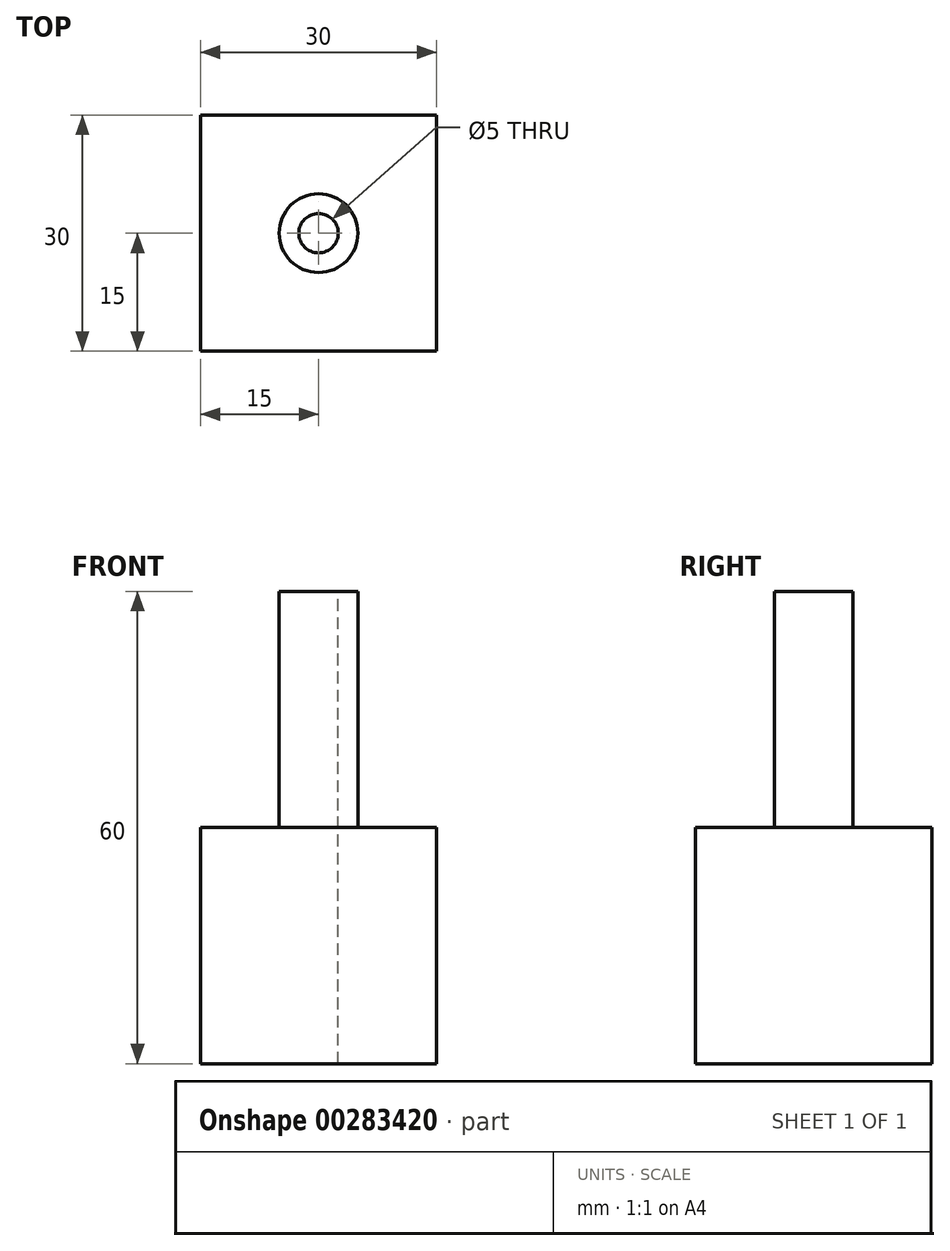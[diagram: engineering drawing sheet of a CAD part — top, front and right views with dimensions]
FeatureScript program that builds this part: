
annotation { "Feature Type Name" : "Feature", "Feature Type Description" : "" }
export const myFeature = defineFeature(function(context is Context, id is Id, definition is map)
    precondition{}
    {
        {
            var Q0;
            Q0=qCreatedBy(makeId("Top.planeOp"),FACE);
            var sketch = newSketch(context, id + "F0", { "sketchPlane" : qUnion([Q0])});
            skLineSegment(sketch, "E0.bottom", {"start": v(15, -15) * mm, "end": v(-15, -15) * mm});
            skLineSegment(sketch, "E0.top", {"start": v(15, 15) * mm, "end": v(-15, 15) * mm});
            skLineSegment(sketch, "E0.left", {"start": v(15, -15) * mm, "end": v(15, 15) * mm});
            skLineSegment(sketch, "E0.right", {"start": v(-15, -15) * mm, "end": v(-15, 15) * mm});
            skPoint(sketch, "E0.middle", {"position": v(0, 0) * mm});
            skSolve(sketch);
        }
        {
            var Q0;
            Q0=makeQuery(id+"F0.imprint","IMPRINT",FACE,{"disambiguationData":[TD([[makeQuery(id+"F0.imprint","IMPRINT",EDGE,{"derivedFrom":sQuery(id+"F0.wireOp",EDGE,"E0.bottom")}),-1.0]])]});
            extrude(context, id + "F1", {"entities" : qUnion([Q0]), "depth" : 30 * mm});
        }
        {
            var Q0;
            Q0=makeQuery(id+"F1.opExtrude","CAP_FACE",FACE,{"disambiguationData":[OSD([sQuery(id+"F0.wireOp",EDGE,"E0.bottom"),sQuery(id+"F0.wireOp",EDGE,"E0.top"),sQuery(id+"F0.wireOp",EDGE,"E0.left"),sQuery(id+"F0.wireOp",EDGE,"E0.right")])],"isStart":false});
            var sketch = newSketch(context, id + "F2", { "sketchPlane" : qUnion([Q0])});
            skCircle(sketch, "E1", {"center": v(0, 0) * mm, "radius": 5 * mm});
            skSolve(sketch);
        }
        {
            var Q0;
            Q0=makeQuery(id+"F2.imprint","IMPRINT",FACE,{"disambiguationData":[TD([[makeQuery(id+"F2.imprint","IMPRINT",EDGE,{"derivedFrom":sQuery(id+"F2.wireOp",EDGE,"E1")}),1.0]])]});
            extrude(context, id + "F3", {"entities" : qUnion([Q0]), "operationType" : NewBodyOperationType.ADD, "depth" : 30 * mm});
        }
        {
            var Q0;
            Q0=makeQuery(id+"F3.opExtrude","CAP_FACE",FACE,{"disambiguationData":[OSD([sQuery(id+"F2.wireOp",EDGE,"E1")])],"isStart":false});
            var sketch = newSketch(context, id + "F4", { "sketchPlane" : qUnion([Q0])});
            skCircle(sketch, "E2", {"center": v(0, 0) * mm, "radius": 2.5 * mm});
            skSolve(sketch);
        }
        {
            var Q0;
            Q0=makeQuery(id+"F4.imprint","IMPRINT",FACE,{"disambiguationData":[TD([[makeQuery(id+"F4.imprint","IMPRINT",EDGE,{"derivedFrom":sQuery(id+"F4.wireOp",EDGE,"E2")}),1.0]])]});
            extrude(context, id + "F5", {"entities" : qUnion([Q0]), "operationType" : NewBodyOperationType.REMOVE, "endBound" : BoundingType.THROUGH_ALL, "oppositeDirection" : true, "depth" : 25 * mm});
        }
    });
